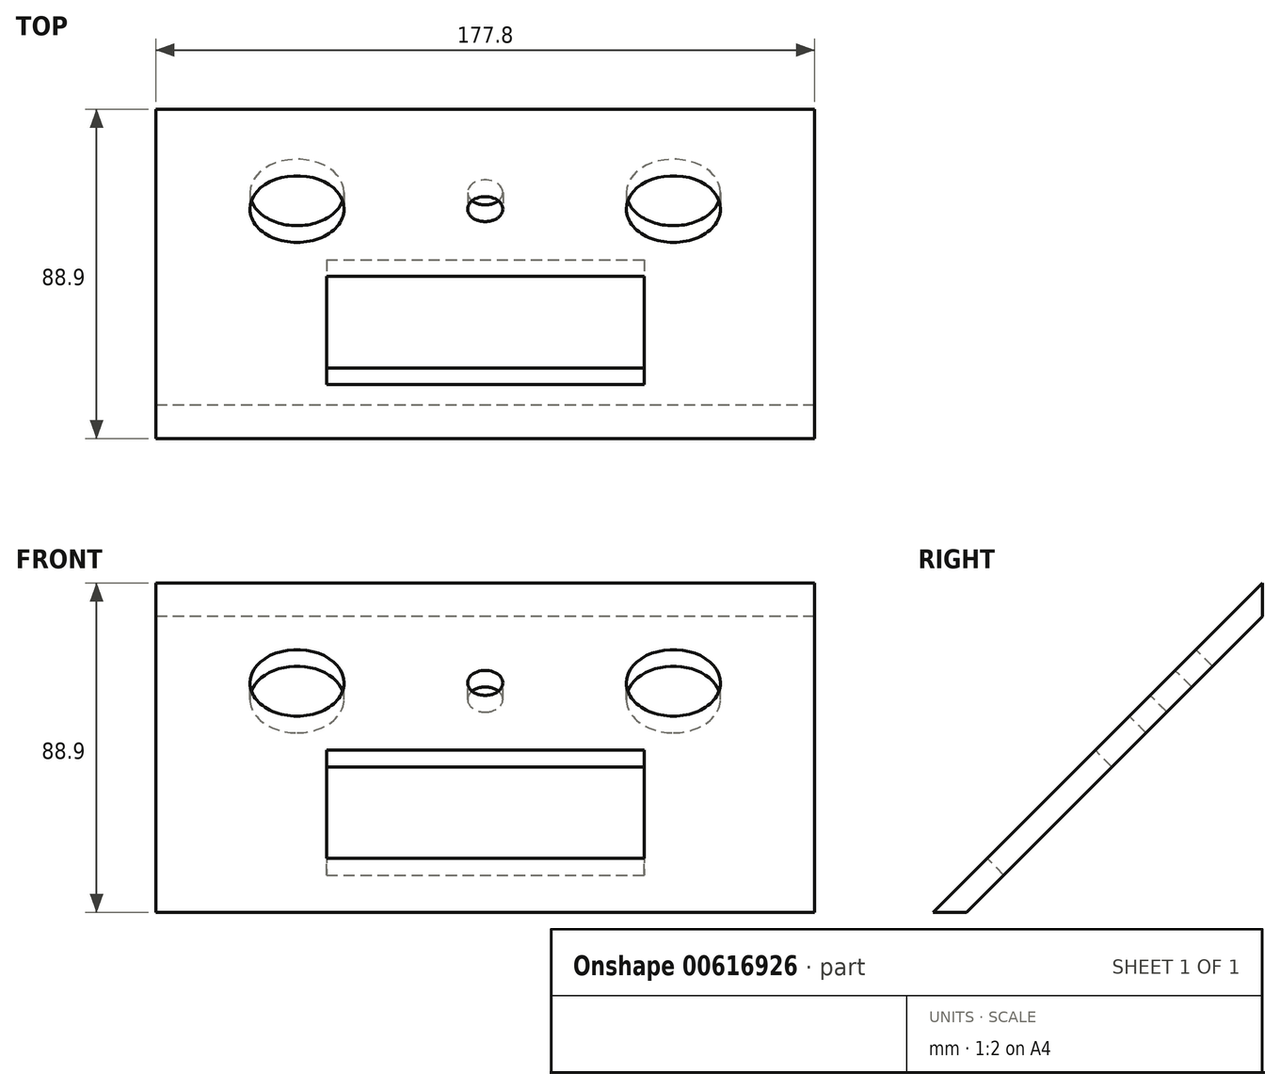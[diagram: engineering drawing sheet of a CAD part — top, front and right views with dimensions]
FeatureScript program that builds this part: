
annotation { "Feature Type Name" : "Feature", "Feature Type Description" : "" }
export const myFeature = defineFeature(function(context is Context, id is Id, definition is map)
    precondition{}
    {
        {
            var Q0;
            Q0=qCreatedBy(makeId("Right.planeOp"),FACE);
            var sketch = newSketch(context, id + "F0", { "sketchPlane" : qUnion([Q0])});
            skLineSegment(sketch, "E0", {"start": v(0, 0) * mm, "end": v(8.98, 0) * mm});
            skLineSegment(sketch, "E1", {"start": v(8.98, 0) * mm, "end": v(88.9, 79.92) * mm});
            skLineSegment(sketch, "E2", {"start": v(88.9, 79.92) * mm, "end": v(88.9, 88.9) * mm});
            skLineSegment(sketch, "E3", {"start": v(88.9, 88.9) * mm, "end": v(0, 0) * mm});
            skLineSegment(sketch, "E4.bottom", {"start": v(0, 0) * mm, "end": v(88.9, 0) * mm, "construction": true});
            skLineSegment(sketch, "E4.top", {"start": v(0, 88.9) * mm, "end": v(88.9, 88.9) * mm, "construction": true});
            skLineSegment(sketch, "E4.left", {"start": v(0, 0) * mm, "end": v(0, 88.9) * mm, "construction": true});
            skLineSegment(sketch, "E4.right", {"start": v(88.9, 0) * mm, "end": v(88.9, 88.9) * mm, "construction": true});
            skSolve(sketch);
        }
        {
            var Q0;
            Q0 = qSketchRegion(id + "F0", true);
            extrude(context, id + "F1", {"entities" : qUnion([Q0]), "endBound" : BoundingType.SYMMETRIC, "depth" : 177.8 * mm, "offsetDistance" : 25.4 * mm});
        }
        {
            var Q0;
            Q0=makeQuery(id+"F1.opExtrude","SWEPT_FACE",FACE,{"disambiguationData":[OSD([sQuery(id+"F0.wireOp",EDGE,"E3")])]});
            var sketch = newSketch(context, id + "F2", { "sketchPlane" : qUnion([Q0])});
            skLineSegment(sketch, "E5.bottom", {"start": v(-88.9, 0) * mm, "end": v(88.9, 0) * mm, "construction": true});
            skLineSegment(sketch, "E5.top", {"start": v(-88.9, 125.72) * mm, "end": v(88.9, 125.72) * mm, "construction": true});
            skLineSegment(sketch, "E5.left", {"start": v(-88.9, 0) * mm, "end": v(-88.9, 125.72) * mm, "construction": true});
            skLineSegment(sketch, "E5.right", {"start": v(88.9, 0) * mm, "end": v(88.9, 125.72) * mm, "construction": true});
            skCircle(sketch, "E6", {"center": v(50.8, 87.62) * mm, "radius": 12.7 * mm});
            skCircle(sketch, "E7", {"center": v(50.8, 87.62) * mm, "radius": 15.88 * mm, "construction": true});
            skCircle(sketch, "E8", {"center": v(-50.8, 87.62) * mm, "radius": 12.7 * mm});
            skCircle(sketch, "E9", {"center": v(-50.8, 87.62) * mm, "radius": 15.88 * mm, "construction": true});
            skLineSegment(sketch, "E10.bottom", {"start": v(-52.39, 71.44) * mm, "end": v(55.56, 71.44) * mm, "construction": true});
            skLineSegment(sketch, "E10.top", {"start": v(-52.39, 11.11) * mm, "end": v(55.56, 11.11) * mm, "construction": true});
            skLineSegment(sketch, "E10.left", {"start": v(-52.39, 71.44) * mm, "end": v(-52.39, 11.11) * mm, "construction": true});
            skLineSegment(sketch, "E10.right", {"start": v(55.56, 71.44) * mm, "end": v(55.56, 11.11) * mm, "construction": true});
            skLineSegment(sketch, "E11.bottom", {"start": v(-42.86, 61.91) * mm, "end": v(42.86, 61.91) * mm});
            skLineSegment(sketch, "E11.top", {"start": v(-42.86, 20.64) * mm, "end": v(42.86, 20.64) * mm});
            skLineSegment(sketch, "E11.left", {"start": v(-42.86, 61.91) * mm, "end": v(-42.86, 20.64) * mm});
            skLineSegment(sketch, "E11.right", {"start": v(42.86, 61.91) * mm, "end": v(42.86, 20.64) * mm});
            skCircle(sketch, "E12", {"center": v(0, 87.62) * mm, "radius": 3.18 * mm, "construction": true});
            skCircle(sketch, "E13", {"center": v(0, 87.62) * mm, "radius": 9.53 * mm, "construction": true});
            skCircle(sketch, "E14", {"center": v(0, 87.62) * mm, "radius": 4.76 * mm});
            skLineSegment(sketch, "E15", {"start": v(-88.9, 87.62) * mm, "end": v(88.9, 87.62) * mm, "construction": true});
            skLineSegment(sketch, "E16", {"start": v(-42.86, 61.91) * mm, "end": v(42.86, 20.64) * mm, "construction": true});
            skLineSegment(sketch, "E17", {"start": v(42.86, 61.91) * mm, "end": v(-42.86, 20.64) * mm, "construction": true});
            skPoint(sketch, "E18", {"position": v(0, 41.28) * mm});
            skSolve(sketch);
        }
        {
            var Q0;
            Q0 = qSketchRegion(id + "F2", true);
            extrude(context, id + "F3", {"entities" : qUnion([Q0]), "operationType" : NewBodyOperationType.REMOVE, "endBound" : BoundingType.THROUGH_ALL, "oppositeDirection" : true, "depth" : 25.4 * mm, "offsetDistance" : 25.4 * mm});
        }
    });
